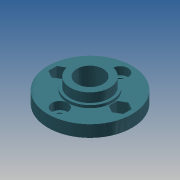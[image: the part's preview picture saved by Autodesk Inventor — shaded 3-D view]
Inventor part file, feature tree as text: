
AUTODESK INVENTOR PART (.ipt)
format: ipt  version: 2013 (Build 170138000, 138)  size: 166,912 bytes
history: native  units: mm
features: extrude x7, sketch x7, pattern_circular x2
ambient origin geometry x8: Origin, YZ Plane, XZ Plane, XY Plane, X Axis, Y Axis, Z Axis, Center Point
bodies: Solid1 (feature_tree)
feature tree (16):
  extrude  "Extrusion1"  Depth=4.5mm TaperAngle=0.0deg
  extrude  "Extrusion2"  Depth=1.0mm TaperAngle=0.0deg
  extrude  "Extrusion3"  Depth=1.0mm TaperAngle=0.0deg
  extrude  "Extrusion4"  Depth=3.5mm
  pattern_circular  "Circular Pattern1"  Count=4 Angle=360.0deg
  extrude  "Extrusion5"  Depth=3.0mm TaperAngle=0.0deg
  extrude  "Extrusion6"  Depth=4.0mm TaperAngle=0.0deg
  pattern_circular  "Circular Pattern2"  Count=2 Angle=360.0deg
  extrude  "Extrusion7"  Depth=10.0mm
  sketch  "Sketch1"  dims[d0=32.0mm d3=4.5mm d4=0.0mm]
  sketch  "Sketch2"  dims[d5=17.0mm d8=1.0mm d9=0.0mm]
  sketch  "Sketch3"  dims[d10=15.0mm d12=1.0mm d13=0.0mm]
  sketch  "Sketch4"  dims[d15=11.5mm d16=3.5mm]
  sketch  "Sketch5"  dims[d17=1.0mm d18=0.0mm d19=40.0mm d20=360.0deg]
  sketch  "Sketch6"  dims[d22=6.0mm d26=3.0mm d27=0.0mm]
  sketch  "Sketch7"  dims[d28=5.5mm d29=4.0mm d30=0.0mm d31=20.0mm d32=360.0deg d34=10.0mm d36=9.0mm d37=0.0mm d40=6.0mm d41=6.0mm]
